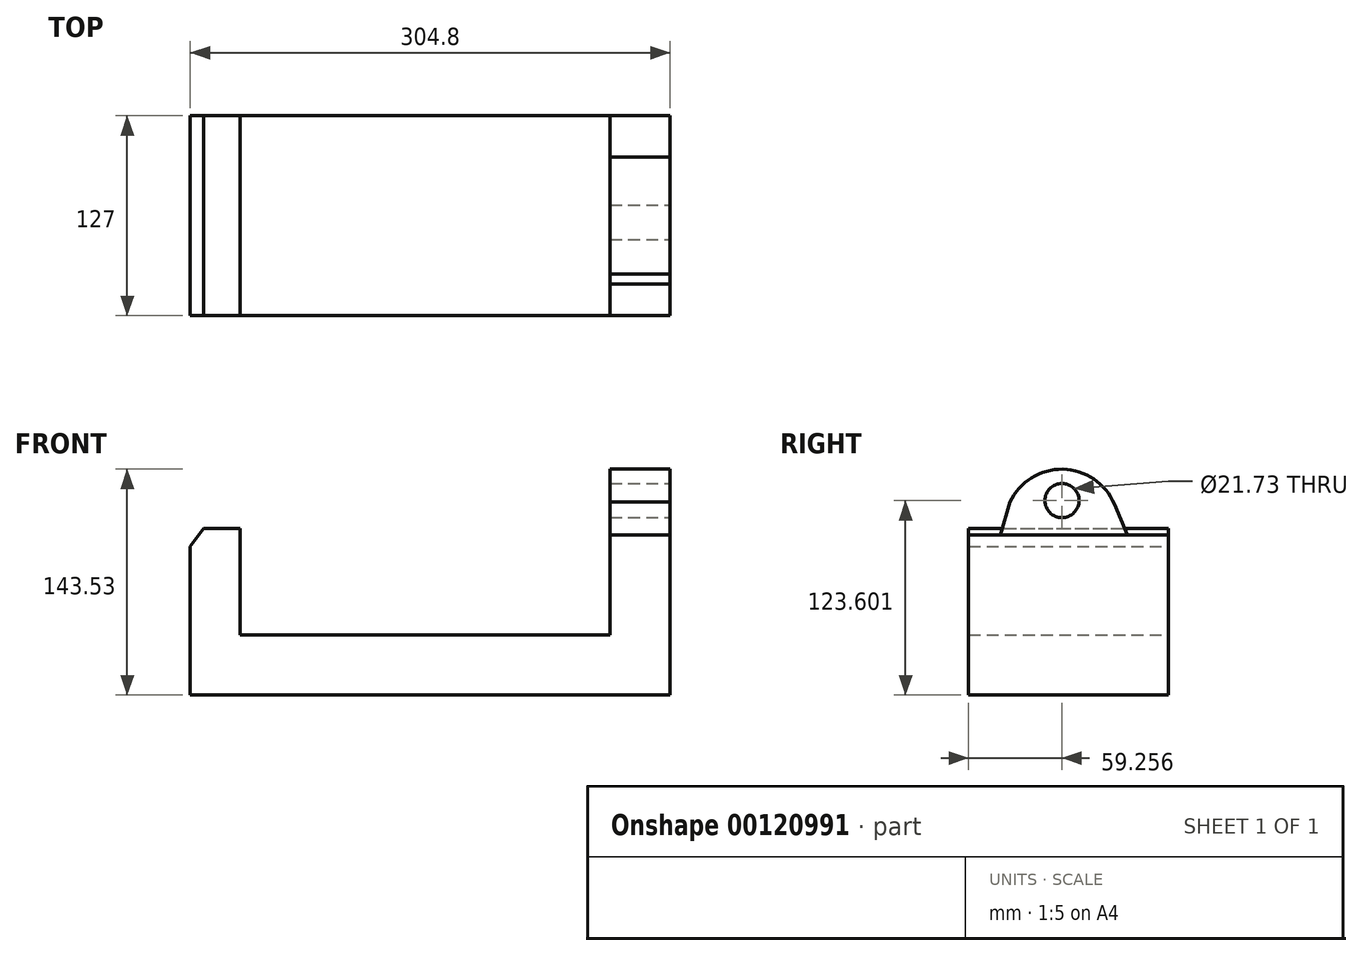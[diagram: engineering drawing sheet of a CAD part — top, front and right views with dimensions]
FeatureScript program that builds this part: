
annotation { "Feature Type Name" : "Feature", "Feature Type Description" : "" }
export const myFeature = defineFeature(function(context is Context, id is Id, definition is map)
    precondition{}
    {
        {
            var Q0;
            Q0=qCreatedBy(makeId("Front.planeOp"),FACE);
            var sketch = newSketch(context, id + "F0", { "sketchPlane" : qUnion([Q0])});
            skLineSegment(sketch, "E0", {"start": v(0, 0) * mm, "end": v(0, 94.45) * mm});
            skLineSegment(sketch, "E1", {"start": v(0, 94.45) * mm, "end": v(8.63, 105.84) * mm});
            skLineSegment(sketch, "E2", {"start": v(8.63, 105.84) * mm, "end": v(31.75, 105.84) * mm});
            skLineSegment(sketch, "E3", {"start": v(31.75, 105.84) * mm, "end": v(31.75, 38.1) * mm});
            skLineSegment(sketch, "E4", {"start": v(31.75, 38.1) * mm, "end": v(266.7, 38.1) * mm});
            skLineSegment(sketch, "E5", {"start": v(266.7, 38.1) * mm, "end": v(266.7, 101.6) * mm});
            skLineSegment(sketch, "E6", {"start": v(266.7, 101.6) * mm, "end": v(304.8, 101.6) * mm});
            skLineSegment(sketch, "E7", {"start": v(304.8, 101.6) * mm, "end": v(304.8, 0) * mm});
            skLineSegment(sketch, "E8", {"start": v(304.8, 0) * mm, "end": v(0, 0) * mm});
            skSolve(sketch);
        }
        {
            var Q0;
            Q0 = qSketchRegion(id + "F0", true);
            extrude(context, id + "F1", {"entities" : qUnion([Q0]), "depth" : 127 * mm});
        }
        {
            var Q0;
            Q0=makeQuery(id+"F1.opExtrude","SWEPT_FACE",FACE,{"disambiguationData":[OSD([sQuery(id+"F0.wireOp",EDGE,"E7")])]});
            var sketch = newSketch(context, id + "F2", { "sketchPlane" : qUnion([Q0])});
            skLineSegment(sketch, "E9", {"start": v(-106.87, 101.6) * mm, "end": v(-100.67, 122.58) * mm});
            skLineSegment(sketch, "E10", {"start": v(-26.23, 101.6) * mm, "end": v(-34.5, 121.34) * mm});
            skArc(sketch, "E11", {"start": v(-34.5, 121.34) * mm, "mid": v(-67.18, 143.53) * mm, "end": v(-100.67, 122.58) * mm});
            skCircle(sketch, "E12", {"center": v(-67.74, 123.6) * mm, "radius": 10.87 * mm});
            skSolve(sketch);
        }
        {
            var Q0;
            {var subQ0=sQuery(id+"F2.wireOp",EDGE,"E9");Q0=makeQuery(id+"F2.imprint","IMPRINT",FACE,{"disambiguationData":[TD([[makeQuery(id+"F2.imprint","IMPRINT",EDGE,{"derivedFrom":subQ0}),-1.0]])]});}
            extrude(context, id + "F3", {"entities" : qUnion([Q0]), "oppositeDirection" : true, "depth" : 38.1 * mm});
        }
    });
